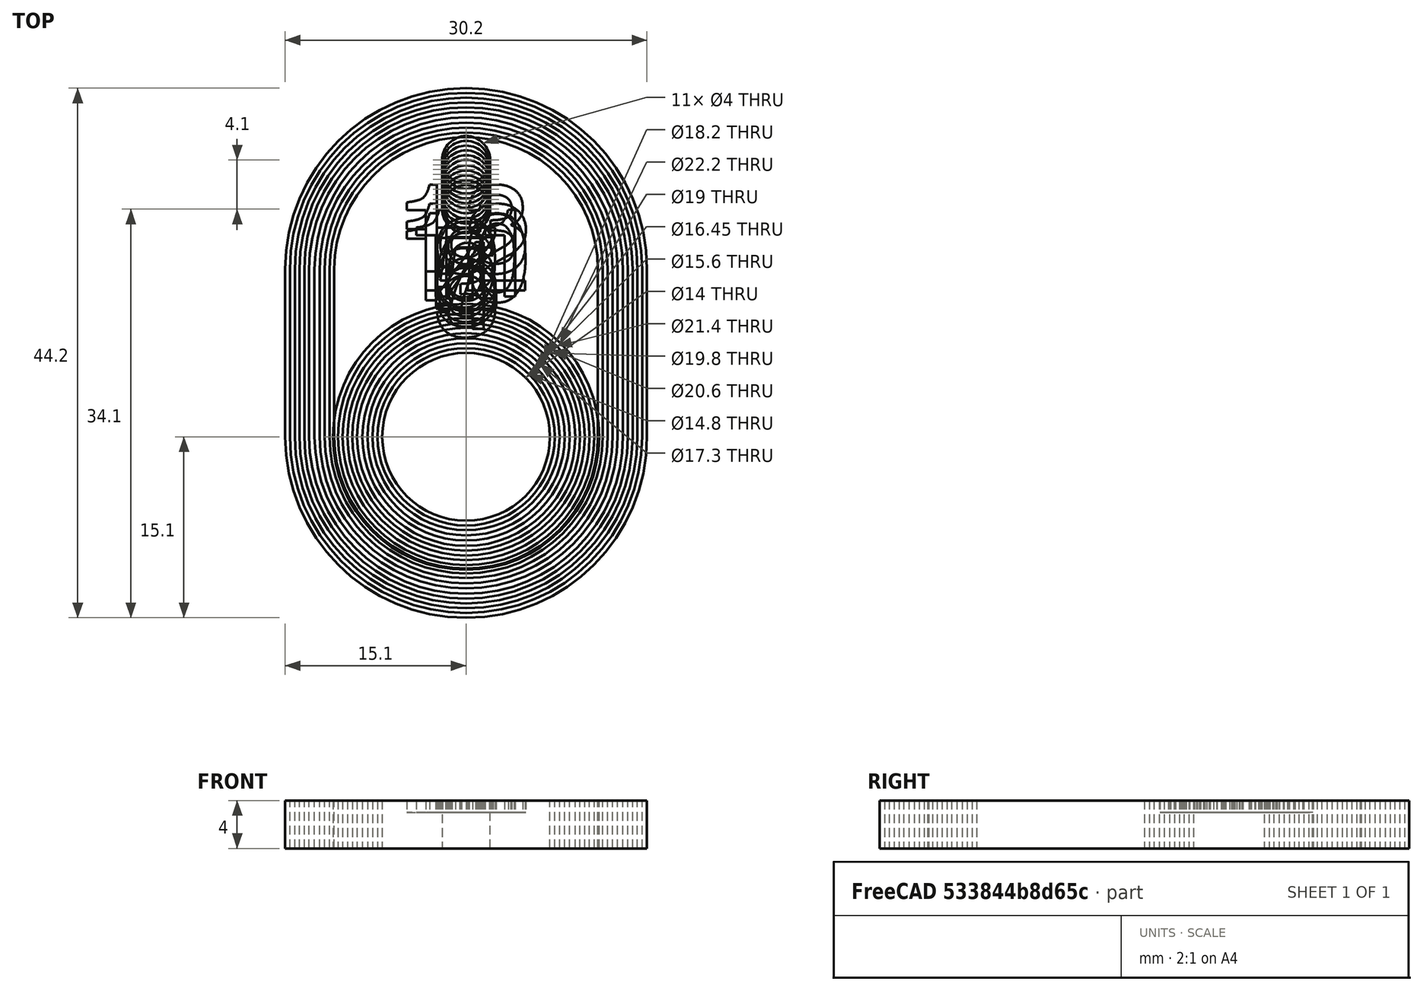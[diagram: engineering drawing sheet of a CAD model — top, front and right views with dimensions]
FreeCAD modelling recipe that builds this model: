
FCSTD DOCUMENT  (FreeCAD 0.18R16146 (Git))
Label: Ring-Gauges
License: All rights reserved
LicenseURL: http://en.wikipedia.org/wiki/All_rights_reserved
objects: Sketcher::SketchObject×22, PartDesign::Pad×11, PartDesign::Pocket×11, PartDesign::Body×11, Mesh::Feature×11, Part::Part2DObjectPython×1
note: 78 computed .brp shape members not serialized (recipe doc carries the construction recipe); baked Part::Feature solids carry a one-line shape summary decoded from their .brp

FEATURE [Sketcher::SketchObject] Sketch  label="Sketch13"
  MapMode = 5
  Support = -> [XY_Plane]
  sketch-geometry (11):
    g0: ArcOfCircle CenterX=-3.8225e-12 CenterY=14 CenterZ=0 NormalX=0 NormalY=0 NormalZ=1 AngleXU=0 Radius=15.1 StartAngle=2.08319e-11 EndAngle=3.14159
    g1: ArcOfCircle CenterX=0 CenterY=0 CenterZ=0 NormalX=0 NormalY=0 NormalZ=1 AngleXU=0 Radius=15.1 StartAngle=3.14159 EndAngle=6.28319
    g2: LineSegment StartX=-15.1 StartY=14 StartZ=0 EndX=-15.1 EndY=-6.47553e-11 EndZ=0
    g3: LineSegment StartX=15.1 StartY=14 StartZ=0 EndX=15.1 EndY=5.34051e-10 EndZ=0
    g4: Circle CenterX=0 CenterY=0 CenterZ=0 NormalX=0 NormalY=0 NormalZ=1 AngleXU=0 Radius=11.1
    g5: Circle CenterX=0 CenterY=23.1 CenterZ=0 NormalX=0 NormalY=0 NormalZ=1 AngleXU=0 Radius=2
    g6: GeomPoint X=0 Y=11.1 Z=0
    g7: GeomPoint X=0 Y=21.1 Z=0
    g8: GeomPoint X=0 Y=29.1 Z=0
    g9: GeomPoint X=0 Y=25.1 Z=0
    g10: GeomPoint X=-11.1 Y=-6.47556e-11 Z=0
  constraints (24):
    c: Tangent(g0,g3) = 1.5708
    c: Tangent(g0,g2) = -1.5708
    c: Tangent(g2,g1) = -1.5708
    c: Tangent(g3,g1) = 1.5708
    c: Vertical(g2)
    c: Equal(g0,g1)
    c: Coincident(g4,g1)
    c: Diameter(g5) = 4
    c: PointOnObject(g6,g4)
    c: Vertical(g6,g1)
    c: PointOnObject(g7,g5)
    c: Vertical(g7,g5)
    c: Vertical(g5,g1)
    c: PointOnObject(g8,g0)
    c: Vertical(g8,g1)
    c: PointOnObject(g9,g5)
    c: Vertical(g9,g5)
    c: DistanceY(g9,g8) = 4
    c: PointOnObject(g10,g4)
    c: Horizontal(g10,g1)
    c: DistanceX(g1,g10) = 4
    c: Diameter(g4) = 22.2
    c: DistanceY(g6,g7) = 10
    c: Coincident(g1,g-1)
FEATURE [PartDesign::Pad] Pad  label="Pad13"
  Length = 4
  Length2 = 100
  Profile = -> Sketch
  Type = 0
FEATURE [Sketcher::SketchObject] Sketch001  label="Sketch12"
  MapMode = 5
  Support = -> [XY_Plane001]
  sketch-geometry (11):
    g0: ArcOfCircle CenterX=-3.88e-14 CenterY=14 CenterZ=0 NormalX=0 NormalY=0 NormalZ=1 AngleXU=0 Radius=14.7 StartAngle=-2.93e-14 EndAngle=3.14159
    g1: ArcOfCircle CenterX=0 CenterY=0 CenterZ=0 NormalX=0 NormalY=0 NormalZ=1 AngleXU=0 Radius=14.7 StartAngle=3.14159 EndAngle=6.28319
    g2: LineSegment StartX=-14.7 StartY=14 StartZ=0 EndX=-14.7 EndY=-2.611e-13 EndZ=0
    g3: LineSegment StartX=14.7 StartY=14 StartZ=0 EndX=14.7 EndY=-7.567e-13 EndZ=0
    g4: Circle CenterX=0 CenterY=0 CenterZ=0 NormalX=0 NormalY=0 NormalZ=1 AngleXU=0 Radius=10.7
    g5: Circle CenterX=0 CenterY=22.7 CenterZ=0 NormalX=0 NormalY=0 NormalZ=1 AngleXU=0 Radius=2
    g6: GeomPoint X=0 Y=10.7 Z=0
    g7: GeomPoint X=0 Y=20.7 Z=0
    g8: GeomPoint X=0 Y=28.7 Z=0
    g9: GeomPoint X=0 Y=24.7 Z=0
    g10: GeomPoint X=-10.7 Y=-2.611e-13 Z=0
  constraints (24):
    c: Tangent(g0,g3) = 1.5708
    c: Tangent(g0,g2) = -1.5708
    c: Tangent(g2,g1) = -1.5708
    c: Tangent(g3,g1) = 1.5708
    c: Vertical(g2)
    c: Equal(g0,g1)
    c: Coincident(g4,g1)
    c: Diameter(g5) = 4
    c: PointOnObject(g6,g4)
    c: Vertical(g6,g1)
    c: PointOnObject(g7,g5)
    c: Vertical(g7,g5)
    c: Vertical(g5,g1)
    c: PointOnObject(g8,g0)
    c: Vertical(g8,g1)
    c: PointOnObject(g9,g5)
    c: Vertical(g9,g5)
    c: DistanceY(g9,g8) = 4
    c: PointOnObject(g10,g4)
    c: Horizontal(g10,g1)
    c: DistanceX(g1,g10) = 4
    c: Diameter(g4) = 21.4
    c: DistanceY(g6,g7) = 10
    c: Coincident(g1,g-1)
FEATURE [PartDesign::Pad] Pad001  label="Pad12"
  Length = 4
  Length2 = 100
  Profile = -> Sketch001
  Type = 0
FEATURE [Sketcher::SketchObject] Sketch002  label="Sketch11"
  MapMode = 5
  Support = -> [XY_Plane002]
  sketch-geometry (11):
    g0: ArcOfCircle CenterX=8e-16 CenterY=14 CenterZ=0 NormalX=0 NormalY=0 NormalZ=1 AngleXU=0 Radius=14.3 StartAngle=1e-16 EndAngle=3.14159
    g1: ArcOfCircle CenterX=0 CenterY=0 CenterZ=0 NormalX=0 NormalY=0 NormalZ=1 AngleXU=0 Radius=14.3 StartAngle=3.14159 EndAngle=6.28319
    g2: LineSegment StartX=-14.3 StartY=14 StartZ=0 EndX=-14.3 EndY=0 EndZ=0
    g3: LineSegment StartX=14.3 StartY=14 StartZ=0 EndX=14.3 EndY=-1.8e-15 EndZ=0
    g4: Circle CenterX=0 CenterY=0 CenterZ=0 NormalX=0 NormalY=0 NormalZ=1 AngleXU=0 Radius=10.3
    g5: Circle CenterX=0 CenterY=22.3 CenterZ=0 NormalX=0 NormalY=0 NormalZ=1 AngleXU=0 Radius=2
    g6: GeomPoint X=0 Y=10.3 Z=0
    g7: GeomPoint X=0 Y=20.3 Z=0
    g8: GeomPoint X=0 Y=28.3 Z=0
    g9: GeomPoint X=0 Y=24.3 Z=0
    g10: GeomPoint X=-10.3 Y=0 Z=0
  constraints (24):
    c: Tangent(g0,g3) = 1.5708
    c: Tangent(g0,g2) = -1.5708
    c: Tangent(g2,g1) = -1.5708
    c: Tangent(g3,g1) = 1.5708
    c: Vertical(g2)
    c: Equal(g0,g1)
    c: Coincident(g4,g1)
    c: Diameter(g5) = 4
    c: PointOnObject(g6,g4)
    c: Vertical(g6,g1)
    c: PointOnObject(g7,g5)
    c: Vertical(g7,g5)
    c: Vertical(g5,g1)
    c: PointOnObject(g8,g0)
    c: Vertical(g8,g1)
    c: PointOnObject(g9,g5)
    c: Vertical(g9,g5)
    c: DistanceY(g9,g8) = 4
    c: PointOnObject(g10,g4)
    c: Horizontal(g10,g1)
    c: DistanceX(g1,g10) = 4
    c: Diameter(g4) = 20.6
    c: DistanceY(g6,g7) = 10
    c: Coincident(g1,g-1)
FEATURE [PartDesign::Pad] Pad003  label="Pad11"
  Length = 4
  Length2 = 100
  Profile = -> Sketch002
  Type = 0
FEATURE [Sketcher::SketchObject] Sketch003  label="Sketch10"
  MapMode = 5
  Support = -> [XY_Plane003]
  sketch-geometry (11):
    g0: ArcOfCircle CenterX=-3.3e-15 CenterY=14 CenterZ=0 NormalX=0 NormalY=0 NormalZ=1 AngleXU=0 Radius=13.9 StartAngle=-1.8e-15 EndAngle=3.14159
    g1: ArcOfCircle CenterX=0 CenterY=0 CenterZ=0 NormalX=0 NormalY=0 NormalZ=1 AngleXU=0 Radius=13.9 StartAngle=3.14159 EndAngle=6.28319
    g2: LineSegment StartX=-13.9 StartY=14 StartZ=0 EndX=-13.9 EndY=-2.66e-14 EndZ=0
    g3: LineSegment StartX=13.9 StartY=14 StartZ=0 EndX=13.9 EndY=-5.33e-14 EndZ=0
    g4: Circle CenterX=0 CenterY=0 CenterZ=0 NormalX=0 NormalY=0 NormalZ=1 AngleXU=0 Radius=9.9
    g5: Circle CenterX=0 CenterY=21.9 CenterZ=0 NormalX=0 NormalY=0 NormalZ=1 AngleXU=0 Radius=2
    g6: GeomPoint X=0 Y=9.9 Z=0
    g7: GeomPoint X=0 Y=19.9 Z=0
    g8: GeomPoint X=0 Y=27.9 Z=0
    g9: GeomPoint X=0 Y=23.9 Z=0
    g10: GeomPoint X=-9.9 Y=-2.66e-14 Z=0
  constraints (24):
    c: Tangent(g0,g3) = 1.5708
    c: Tangent(g0,g2) = -1.5708
    c: Tangent(g2,g1) = -1.5708
    c: Tangent(g3,g1) = 1.5708
    c: Vertical(g2)
    c: Equal(g0,g1)
    c: Coincident(g4,g1)
    c: Diameter(g5) = 4
    c: PointOnObject(g6,g4)
    c: Vertical(g6,g1)
    c: PointOnObject(g7,g5)
    c: Vertical(g7,g5)
    c: Vertical(g5,g1)
    c: PointOnObject(g8,g0)
    c: Vertical(g8,g1)
    c: PointOnObject(g9,g5)
    c: Vertical(g9,g5)
    c: DistanceY(g9,g8) = 4
    c: PointOnObject(g10,g4)
    c: Horizontal(g10,g1)
    c: DistanceX(g1,g10) = 4
    c: Diameter(g4) = 19.8
    c: DistanceY(g6,g7) = 10
    c: Coincident(g1,g-1)
FEATURE [PartDesign::Pad] Pad002  label="Pad10"
  Length = 4
  Length2 = 100
  Profile = -> Sketch003
  Type = 0
FEATURE [Sketcher::SketchObject] Sketch004  label="Sketch9"
  MapMode = 5
  Support = -> [XY_Plane004]
  sketch-geometry (11):
    g0: ArcOfCircle CenterX=-5e-16 CenterY=14 CenterZ=0 NormalX=0 NormalY=0 NormalZ=1 AngleXU=0 Radius=13.5 StartAngle=1e-16 EndAngle=3.14159
    g1: ArcOfCircle CenterX=0 CenterY=0 CenterZ=0 NormalX=0 NormalY=0 NormalZ=1 AngleXU=0 Radius=13.5 StartAngle=3.14159 EndAngle=6.28319
    g2: LineSegment StartX=-13.5 StartY=14 StartZ=0 EndX=-13.5 EndY=0 EndZ=0
    g3: LineSegment StartX=13.5 StartY=14 StartZ=0 EndX=13.5 EndY=-1.8e-15 EndZ=0
    g4: Circle CenterX=0 CenterY=0 CenterZ=0 NormalX=0 NormalY=0 NormalZ=1 AngleXU=0 Radius=9.5
    g5: Circle CenterX=0 CenterY=21.5 CenterZ=0 NormalX=0 NormalY=0 NormalZ=1 AngleXU=0 Radius=2
    g6: GeomPoint X=0 Y=9.5 Z=0
    g7: GeomPoint X=0 Y=19.5 Z=0
    g8: GeomPoint X=0 Y=27.5 Z=0
    g9: GeomPoint X=0 Y=23.5 Z=0
    g10: GeomPoint X=-9.5 Y=0 Z=0
  constraints (24):
    c: Tangent(g0,g3) = 1.5708
    c: Tangent(g0,g2) = -1.5708
    c: Tangent(g2,g1) = -1.5708
    c: Tangent(g3,g1) = 1.5708
    c: Vertical(g2)
    c: Equal(g0,g1)
    c: Coincident(g4,g1)
    c: Diameter(g5) = 4
    c: PointOnObject(g6,g4)
    c: Vertical(g6,g1)
    c: PointOnObject(g7,g5)
    c: Vertical(g7,g5)
    c: Vertical(g5,g1)
    c: PointOnObject(g8,g0)
    c: Vertical(g8,g1)
    c: PointOnObject(g9,g5)
    c: Vertical(g9,g5)
    c: DistanceY(g9,g8) = 4
    c: PointOnObject(g10,g4)
    c: Horizontal(g10,g1)
    c: DistanceX(g1,g10) = 4
    c: Diameter(g4) = 19
    c: DistanceY(g6,g7) = 10
    c: Coincident(g1,g-1)
FEATURE [PartDesign::Pad] Pad005  label="Pad9"
  Length = 4
  Length2 = 100
  Profile = -> Sketch004
  Type = 0
FEATURE [Sketcher::SketchObject] Sketch005  label="Sketch8"
  MapMode = 5
  Support = -> [XY_Plane005]
  sketch-geometry (11):
    g0: ArcOfCircle CenterX=5e-16 CenterY=14 CenterZ=0 NormalX=0 NormalY=0 NormalZ=1 AngleXU=0 Radius=13.1 StartAngle=1e-16 EndAngle=3.14159
    g1: ArcOfCircle CenterX=0 CenterY=0 CenterZ=0 NormalX=0 NormalY=0 NormalZ=1 AngleXU=0 Radius=13.1 StartAngle=3.14159 EndAngle=6.28319
    g2: LineSegment StartX=-13.1 StartY=14 StartZ=0 EndX=-13.1 EndY=0 EndZ=0
    g3: LineSegment StartX=13.1 StartY=14 StartZ=0 EndX=13.1 EndY=-3.6e-15 EndZ=0
    g4: Circle CenterX=0 CenterY=0 CenterZ=0 NormalX=0 NormalY=0 NormalZ=1 AngleXU=0 Radius=9.1
    g5: Circle CenterX=0 CenterY=21.1 CenterZ=0 NormalX=0 NormalY=0 NormalZ=1 AngleXU=0 Radius=2
    g6: GeomPoint X=0 Y=9.1 Z=0
    g7: GeomPoint X=0 Y=19.1 Z=0
    g8: GeomPoint X=0 Y=27.1 Z=0
    g9: GeomPoint X=0 Y=23.1 Z=0
    g10: GeomPoint X=-9.1 Y=0 Z=0
  constraints (24):
    c: Tangent(g0,g3) = 1.5708
    c: Tangent(g0,g2) = -1.5708
    c: Tangent(g2,g1) = -1.5708
    c: Tangent(g3,g1) = 1.5708
    c: Vertical(g2)
    c: Equal(g0,g1)
    c: Coincident(g4,g1)
    c: Diameter(g5) = 4
    c: PointOnObject(g6,g4)
    c: Vertical(g6,g1)
    c: PointOnObject(g7,g5)
    c: Vertical(g7,g5)
    c: Vertical(g5,g1)
    c: PointOnObject(g8,g0)
    c: Vertical(g8,g1)
    c: PointOnObject(g9,g5)
    c: Vertical(g9,g5)
    c: DistanceY(g9,g8) = 4
    c: PointOnObject(g10,g4)
    c: Horizontal(g10,g1)
    c: DistanceX(g1,g10) = 4
    c: Diameter(g4) = 18.2
    c: DistanceY(g6,g7) = 10
    c: Coincident(g1,g-1)
FEATURE [PartDesign::Pad] Pad004  label="Pad8"
  Length = 4
  Length2 = 100
  Profile = -> Sketch005
  Type = 0
FEATURE [Sketcher::SketchObject] Sketch006  label="Sketch7"
  MapMode = 5
  Support = -> [XY_Plane006]
  sketch-geometry (11):
    g0: ArcOfCircle CenterX=0 CenterY=14 CenterZ=0 NormalX=0 NormalY=0 NormalZ=1 AngleXU=0 Radius=12.65 StartAngle=0 EndAngle=3.14159
    g1: ArcOfCircle CenterX=0 CenterY=0 CenterZ=0 NormalX=0 NormalY=0 NormalZ=1 AngleXU=0 Radius=12.65 StartAngle=3.14159 EndAngle=6.28319
    g2: LineSegment StartX=-12.65 StartY=14 StartZ=0 EndX=-12.65 EndY=1.8e-15 EndZ=0
    g3: LineSegment StartX=12.65 StartY=14 StartZ=0 EndX=12.65 EndY=-3.6e-15 EndZ=0
    g4: Circle CenterX=0 CenterY=0 CenterZ=0 NormalX=0 NormalY=0 NormalZ=1 AngleXU=0 Radius=8.65
    g5: Circle CenterX=0 CenterY=20.65 CenterZ=0 NormalX=0 NormalY=0 NormalZ=1 AngleXU=0 Radius=2
    g6: GeomPoint X=0 Y=8.65 Z=0
    g7: GeomPoint X=0 Y=18.65 Z=0
    g8: GeomPoint X=0 Y=26.65 Z=0
    g9: GeomPoint X=0 Y=22.65 Z=0
    g10: GeomPoint X=-8.65 Y=1.5e-15 Z=0
  constraints (24):
    c: Tangent(g0,g3) = 1.5708
    c: Tangent(g0,g2) = -1.5708
    c: Tangent(g2,g1) = -1.5708
    c: Tangent(g3,g1) = 1.5708
    c: Vertical(g2)
    c: Equal(g0,g1)
    c: Coincident(g4,g1)
    c: Diameter(g5) = 4
    c: PointOnObject(g6,g4)
    c: Vertical(g6,g1)
    c: PointOnObject(g7,g5)
    c: Vertical(g7,g5)
    c: Vertical(g5,g1)
    c: PointOnObject(g8,g0)
    c: Vertical(g8,g1)
    c: PointOnObject(g9,g5)
    c: Vertical(g9,g5)
    c: DistanceY(g9,g8) = 4
    c: PointOnObject(g10,g4)
    c: Horizontal(g10,g1)
    c: DistanceX(g1,g10) = 4
    c: Diameter(g4) = 17.3
    c: DistanceY(g6,g7) = 10
    c: Coincident(g1,g-1)
FEATURE [PartDesign::Pad] Pad007  label="Pad7"
  Length = 4
  Length2 = 100
  Profile = -> Sketch006
  Type = 0
FEATURE [Sketcher::SketchObject] Sketch007  label="Sketch6"
  MapMode = 5
  Support = -> [XY_Plane007]
  sketch-geometry (11):
    g0: ArcOfCircle CenterX=-1.3e-15 CenterY=14 CenterZ=0 NormalX=0 NormalY=0 NormalZ=1 AngleXU=0 Radius=12.225 StartAngle=-3.6e-15 EndAngle=3.14159
    g1: ArcOfCircle CenterX=0 CenterY=0 CenterZ=0 NormalX=0 NormalY=0 NormalZ=1 AngleXU=0 Radius=12.225 StartAngle=3.14159 EndAngle=6.28319
    g2: LineSegment StartX=-12.225 StartY=14 StartZ=0 EndX=-12.225 EndY=1.8e-15 EndZ=0
    g3: LineSegment StartX=12.225 StartY=14 StartZ=0 EndX=12.225 EndY=-4.62e-14 EndZ=0
    g4: Circle CenterX=0 CenterY=0 CenterZ=0 NormalX=0 NormalY=0 NormalZ=1 AngleXU=0 Radius=8.225
    g5: Circle CenterX=0 CenterY=20.225 CenterZ=0 NormalX=0 NormalY=0 NormalZ=1 AngleXU=0 Radius=2
    g6: GeomPoint X=0 Y=8.225 Z=0
    g7: GeomPoint X=0 Y=18.225 Z=0
    g8: GeomPoint X=0 Y=26.225 Z=0
    g9: GeomPoint X=0 Y=22.225 Z=0
    g10: GeomPoint X=-8.225 Y=1.5e-15 Z=0
  constraints (24):
    c: Tangent(g0,g3) = 1.5708
    c: Tangent(g0,g2) = -1.5708
    c: Tangent(g2,g1) = -1.5708
    c: Tangent(g3,g1) = 1.5708
    c: Vertical(g2)
    c: Equal(g0,g1)
    c: Coincident(g4,g1)
    c: Diameter(g5) = 4
    c: PointOnObject(g6,g4)
    c: Vertical(g6,g1)
    c: PointOnObject(g7,g5)
    c: Vertical(g7,g5)
    c: Vertical(g5,g1)
    c: PointOnObject(g8,g0)
    c: Vertical(g8,g1)
    c: PointOnObject(g9,g5)
    c: Vertical(g9,g5)
    c: DistanceY(g9,g8) = 4
    c: PointOnObject(g10,g4)
    c: Horizontal(g10,g1)
    c: DistanceX(g1,g10) = 4
    c: Diameter(g4) = 16.45
    c: DistanceY(g6,g7) = 10
    c: Coincident(g1,g-1)
FEATURE [PartDesign::Pad] Pad006  label="Pad6"
  Length = 4
  Length2 = 100
  Profile = -> Sketch007
  Type = 0
FEATURE [Sketcher::SketchObject] Sketch008  label="Sketch5"
  MapMode = 5
  Support = -> [XY_Plane008]
  sketch-geometry (11):
    g0: ArcOfCircle CenterX=-4.8e-15 CenterY=14 CenterZ=0 NormalX=0 NormalY=0 NormalZ=1 AngleXU=0 Radius=11.8 StartAngle=-4.09e-14 EndAngle=3.14159
    g1: ArcOfCircle CenterX=0 CenterY=0 CenterZ=0 NormalX=0 NormalY=0 NormalZ=1 AngleXU=0 Radius=11.8 StartAngle=3.14159 EndAngle=6.28319
    g2: LineSegment StartX=-11.8 StartY=14 StartZ=0 EndX=-11.8 EndY=4.8e-14 EndZ=0
    g3: LineSegment StartX=11.8 StartY=14 StartZ=0 EndX=11.8 EndY=-2.167e-13 EndZ=0
    g4: Circle CenterX=0 CenterY=0 CenterZ=0 NormalX=0 NormalY=0 NormalZ=1 AngleXU=0 Radius=7.8
    g5: Circle CenterX=0 CenterY=19.8 CenterZ=0 NormalX=0 NormalY=0 NormalZ=1 AngleXU=0 Radius=2
    g6: GeomPoint X=0 Y=7.8 Z=0
    g7: GeomPoint X=0 Y=17.8 Z=0
    g8: GeomPoint X=0 Y=25.8 Z=0
    g9: GeomPoint X=0 Y=21.8 Z=0
    g10: GeomPoint X=-7.8 Y=4.86e-14 Z=0
  constraints (24):
    c: Tangent(g0,g3) = 1.5708
    c: Tangent(g0,g2) = -1.5708
    c: Tangent(g2,g1) = -1.5708
    c: Tangent(g3,g1) = 1.5708
    c: Vertical(g2)
    c: Equal(g0,g1)
    c: Coincident(g4,g1)
    c: Diameter(g5) = 4
    c: PointOnObject(g6,g4)
    c: Vertical(g6,g1)
    c: PointOnObject(g7,g5)
    c: Vertical(g7,g5)
    c: Vertical(g5,g1)
    c: PointOnObject(g8,g0)
    c: Vertical(g8,g1)
    c: PointOnObject(g9,g5)
    c: Vertical(g9,g5)
    c: DistanceY(g9,g8) = 4
    c: PointOnObject(g10,g4)
    c: Horizontal(g10,g1)
    c: DistanceX(g1,g10) = 4
    c: Diameter(g4) = 15.6
    c: DistanceY(g6,g7) = 10
    c: Coincident(g1,g-1)
FEATURE [PartDesign::Pad] Pad009  label="Pad5"
  Length = 4
  Length2 = 100
  Profile = -> Sketch008
  Type = 0
FEATURE [Sketcher::SketchObject] Sketch009  label="Sketch4"
  MapMode = 5
  Support = -> [XY_Plane009]
  sketch-geometry (11):
    g0: ArcOfCircle CenterX=-5e-16 CenterY=14 CenterZ=0 NormalX=0 NormalY=0 NormalZ=1 AngleXU=0 Radius=11.4 StartAngle=1e-16 EndAngle=3.14159
    g1: ArcOfCircle CenterX=0 CenterY=0 CenterZ=0 NormalX=0 NormalY=0 NormalZ=1 AngleXU=0 Radius=11.4 StartAngle=3.14159 EndAngle=6.28319
    g2: LineSegment StartX=-11.4 StartY=14 StartZ=0 EndX=-11.4 EndY=0 EndZ=0
    g3: LineSegment StartX=11.4 StartY=14 StartZ=0 EndX=11.4 EndY=-3.6e-15 EndZ=0
    g4: Circle CenterX=0 CenterY=0 CenterZ=0 NormalX=0 NormalY=0 NormalZ=1 AngleXU=0 Radius=7.4
    g5: Circle CenterX=0 CenterY=19.4 CenterZ=0 NormalX=0 NormalY=0 NormalZ=1 AngleXU=0 Radius=2
    g6: GeomPoint X=0 Y=7.4 Z=0
    g7: GeomPoint X=0 Y=17.4 Z=0
    g8: GeomPoint X=0 Y=25.4 Z=0
    g9: GeomPoint X=0 Y=21.4 Z=0
    g10: GeomPoint X=-7.4 Y=0 Z=0
  constraints (24):
    c: Tangent(g0,g3) = 1.5708
    c: Tangent(g0,g2) = -1.5708
    c: Tangent(g2,g1) = -1.5708
    c: Tangent(g3,g1) = 1.5708
    c: Vertical(g2)
    c: Equal(g0,g1)
    c: Coincident(g4,g1)
    c: Diameter(g5) = 4
    c: PointOnObject(g6,g4)
    c: Vertical(g6,g1)
    c: PointOnObject(g7,g5)
    c: Vertical(g7,g5)
    c: Vertical(g5,g1)
    c: PointOnObject(g8,g0)
    c: Vertical(g8,g1)
    c: PointOnObject(g9,g5)
    c: Vertical(g9,g5)
    c: DistanceY(g9,g8) = 4
    c: PointOnObject(g10,g4)
    c: Horizontal(g10,g1)
    c: DistanceX(g1,g10) = 4
    c: Diameter(g4) = 14.8
    c: DistanceY(g6,g7) = 10
    c: Coincident(g1,g-1)
FEATURE [PartDesign::Pad] Pad008  label="Pad4"
  Length = 4
  Length2 = 100
  Profile = -> Sketch009
  Type = 0
FEATURE [Sketcher::SketchObject] Sketch010  label="Sketch3"
  MapMode = 5
  Support = -> [XY_Plane010]
  sketch-geometry (11):
    g0: ArcOfCircle CenterX=3e-16 CenterY=14 CenterZ=0 NormalX=0 NormalY=0 NormalZ=1 AngleXU=0 Radius=11 StartAngle=3.8e-15 EndAngle=3.14159
    g1: ArcOfCircle CenterX=0 CenterY=0 CenterZ=0 NormalX=0 NormalY=0 NormalZ=1 AngleXU=0 Radius=11 StartAngle=3.14159 EndAngle=6.28319
    g2: LineSegment StartX=-11 StartY=14 StartZ=0 EndX=-11 EndY=0 EndZ=0
    g3: LineSegment StartX=11 StartY=14 StartZ=0 EndX=11 EndY=7.1e-15 EndZ=0
    g4: Circle CenterX=0 CenterY=0 CenterZ=0 NormalX=0 NormalY=0 NormalZ=1 AngleXU=0 Radius=7
    g5: Circle CenterX=0 CenterY=19 CenterZ=0 NormalX=0 NormalY=0 NormalZ=1 AngleXU=0 Radius=2
    g6: GeomPoint X=0 Y=7 Z=0
    g7: GeomPoint X=0 Y=17 Z=0
    g8: GeomPoint X=0 Y=25 Z=0
    g9: GeomPoint X=0 Y=21 Z=0
    g10: GeomPoint X=-7 Y=5e-16 Z=0
  constraints (24):
    c: Tangent(g0,g3) = 1.5708
    c: Tangent(g0,g2) = -1.5708
    c: Tangent(g2,g1) = -1.5708
    c: Tangent(g3,g1) = 1.5708
    c: Vertical(g2)
    c: Equal(g0,g1)
    c: Coincident(g4,g1)
    c: Diameter(g5) = 4
    c: PointOnObject(g6,g4)
    c: Vertical(g6,g1)
    c: PointOnObject(g7,g5)
    c: Vertical(g7,g5)
    c: Vertical(g5,g1)
    c: PointOnObject(g8,g0)
    c: Vertical(g8,g1)
    c: PointOnObject(g9,g5)
    c: Vertical(g9,g5)
    c: DistanceY(g9,g8) = 4
    c: PointOnObject(g10,g4)
    c: Horizontal(g10,g1)
    c: DistanceX(g1,g10) = 4
    c: Diameter(g4) = 14
    c: DistanceY(g6,g7) = 10
    c: Coincident(g1,g-1)
FEATURE [PartDesign::Pad] Pad011  label="Pad3"
  Length = 4
  Length2 = 100
  Profile = -> Sketch010
  Type = 0
FEATURE [Part::Part2DObjectPython] ShapeString  label="Draft-Number"  # Draft 2D object (typed FeaturePython)
  FontFile = <path>
  Placement = pos=(-30,20,0) rot=(0,0,1;0rad)
  Size = 4
  String = 13
  Tracking = 0
FEATURE [Sketcher::SketchObject] CopySketch011  label="Num3"
  Placement = pos=(27.25,-11.5,4) rot=(0,0,1;0rad)
  sketch-geometry (25):
    g0: BSplineCurve PolesCount=3 KnotsCount=2 Degree=2 IsPeriodic=0
    g1: BSplineCurve PolesCount=3 KnotsCount=2 Degree=2 IsPeriodic=0
    g2: BSplineCurve PolesCount=3 KnotsCount=2 Degree=2 IsPeriodic=0
    g3: BSplineCurve PolesCount=3 KnotsCount=2 Degree=2 IsPeriodic=0
    g4: BSplineCurve PolesCount=3 KnotsCount=2 Degree=2 IsPeriodic=0
    g5: LineSegment StartX=-27.7367 StartY=23.4133 StartZ=0 EndX=-27.7367 EndY=24.2667 EndZ=0
    g6: LineSegment StartX=-27.6233 StartY=23.4133 StartZ=0 EndX=-27.7367 EndY=23.4133 EndZ=0
    g7: LineSegment StartX=-27.2433 StartY=23.4233 StartZ=0 EndX=-27.6233 EndY=23.4133 EndZ=0
    g8: BSplineCurve PolesCount=3 KnotsCount=2 Degree=2 IsPeriodic=0
    g9: BSplineCurve PolesCount=3 KnotsCount=2 Degree=2 IsPeriodic=0
    g10: BSplineCurve PolesCount=3 KnotsCount=2 Degree=2 IsPeriodic=0
    g11: BSplineCurve PolesCount=3 KnotsCount=2 Degree=2 IsPeriodic=0
    g12: BSplineCurve PolesCount=3 KnotsCount=2 Degree=2 IsPeriodic=0
    g13: LineSegment StartX=-29.6733 StartY=21.92 StartZ=0 EndX=-28.77 EndY=21.92 EndZ=0
    g14: BSplineCurve PolesCount=3 KnotsCount=2 Degree=2 IsPeriodic=0
    g15: BSplineCurve PolesCount=3 KnotsCount=2 Degree=2 IsPeriodic=0
    g16: BSplineCurve PolesCount=3 KnotsCount=2 Degree=2 IsPeriodic=0
    g17: BSplineCurve PolesCount=3 KnotsCount=2 Degree=2 IsPeriodic=0
    g18: BSplineCurve PolesCount=3 KnotsCount=2 Degree=2 IsPeriodic=0
    g19: BSplineCurve PolesCount=3 KnotsCount=2 Degree=2 IsPeriodic=0
    g20: BSplineCurve PolesCount=3 KnotsCount=2 Degree=2 IsPeriodic=0
    g21: BSplineCurve PolesCount=3 KnotsCount=2 Degree=2 IsPeriodic=0
    g22: BSplineCurve PolesCount=3 KnotsCount=2 Degree=2 IsPeriodic=0
    g23: LineSegment StartX=-28.6167 StartY=25.12 StartZ=0 EndX=-29.52 EndY=25.12 EndZ=0
    g24: BSplineCurve PolesCount=3 KnotsCount=2 Degree=2 IsPeriodic=0
  constraints (29):
    c: Coincident(g0,g1)
    c: Coincident(g1,g2)
    c: Coincident(g2,g3)
    c: Coincident(g3,g4)
    c: Coincident(g4,g5)
    c: Vertical(g5)
    c: Coincident(g5,g6)
    c: Horizontal(g6)
    c: Coincident(g6,g7)
    c: Coincident(g7,g8)
    c: Coincident(g8,g9)
    c: Coincident(g9,g10)
    c: Coincident(g10,g11)
    c: Coincident(g11,g12)
    c: Coincident(g12,g13)
    c: Horizontal(g13)
    c: Coincident(g13,g14)
    c: Coincident(g14,g15)
    c: Coincident(g15,g16)
    c: Coincident(g16,g17)
    c: Coincident(g17,g18)
    c: Coincident(g18,g19)
    c: Coincident(g19,g20)
    c: Coincident(g20,g21)
    c: Coincident(g21,g22)
    c: Coincident(g22,g23)
    c: Horizontal(g23)
    c: Coincident(g23,g24)
    c: Coincident(g24,g0)
FEATURE [PartDesign::Pocket] Pocket  label="Pocket3"
  BaseFeature = -> Pad011
  Length = 1
  Length2 = 100
  Profile = -> CopySketch011
  Type = 0
FEATURE [PartDesign::Body] Body010  label="Size-3"
  Group = -> [Sketch010,Pad011,Pocket]
  Origin = -> Origin010
  Tip = -> Pocket
FEATURE [Sketcher::SketchObject] Sketch011  label="Num4"
  AttachmentOffset = pos=(27.2,-11,0) rot=(0,0,1;0rad)
  MapMode = 5
  Placement = pos=(27.2,-11,4) rot=(0,0,1;0rad)
  Support = -> [Pad008]
  sketch-geometry (14):
    g0: LineSegment StartX=-26.65 StartY=21.7067 StartZ=0 EndX=-29.7133 EndY=21.7067 EndZ=0
    g1: LineSegment StartX=-26.65 StartY=20 StartZ=0 EndX=-26.65 EndY=21.7067 EndZ=0
    g2: LineSegment StartX=-25.75 StartY=20 StartZ=0 EndX=-26.65 EndY=20 EndZ=0
    g3: LineSegment StartX=-25.75 StartY=21.7067 StartZ=0 EndX=-25.75 EndY=20 EndZ=0
    g4: LineSegment StartX=-24.6767 StartY=21.7067 StartZ=0 EndX=-25.75 EndY=21.7067 EndZ=0
    g5: LineSegment StartX=-24.6767 StartY=22.56 StartZ=0 EndX=-24.6767 EndY=21.7067 EndZ=0
    g6: LineSegment StartX=-25.75 StartY=22.56 StartZ=0 EndX=-24.6767 EndY=22.56 EndZ=0
    g7: LineSegment StartX=-25.75 StartY=27.2533 StartZ=0 EndX=-25.75 EndY=22.56 EndZ=0
    g8: LineSegment StartX=-26.4167 StartY=27.2533 StartZ=0 EndX=-25.75 EndY=27.2533 EndZ=0
    g9: LineSegment StartX=-29.7133 StartY=22.7033 StartZ=0 EndX=-26.4167 EndY=27.2533 EndZ=0
    g10: LineSegment StartX=-29.7133 StartY=21.7067 StartZ=0 EndX=-29.7133 EndY=22.7033 EndZ=0
    g11: LineSegment StartX=-26.65 StartY=22.56 StartZ=0 EndX=-26.65 EndY=25.7233 EndZ=0
    g12: LineSegment StartX=-28.9233 StartY=22.56 StartZ=0 EndX=-26.65 EndY=22.56 EndZ=0
    g13: LineSegment StartX=-26.65 StartY=25.7233 StartZ=0 EndX=-28.9233 EndY=22.56 EndZ=0
  constraints (26):
    c: Horizontal(g0)
    c: Coincident(g0,g1)
    c: Vertical(g1)
    c: Coincident(g1,g2)
    c: Horizontal(g2)
    c: Coincident(g2,g3)
    c: Vertical(g3)
    c: Coincident(g3,g4)
    c: Horizontal(g4)
    c: Coincident(g4,g5)
    c: Vertical(g5)
    c: Coincident(g5,g6)
    c: Horizontal(g6)
    c: Coincident(g6,g7)
    c: Vertical(g7)
    c: Coincident(g7,g8)
    c: Horizontal(g8)
    c: Coincident(g8,g9)
    c: Coincident(g9,g10)
    c: Vertical(g10)
    c: Coincident(g10,g0)
    c: Vertical(g11)
    c: Coincident(g11,g12)
    c: Horizontal(g12)
    c: Coincident(g12,g13)
    c: Coincident(g13,g11)
FEATURE [PartDesign::Pocket] Pocket001  label="Pocket4"
  BaseFeature = -> Pad008
  Length = 1
  Length2 = 100
  Profile = -> Sketch011
  Type = 0
FEATURE [PartDesign::Body] Body009  label="Size-4"
  Group = -> [Sketch009,Pad008,Sketch011,Pocket001]
  Origin = -> Origin009
  Tip = -> Pocket001
FEATURE [Sketcher::SketchObject] Sketch012  label="Num5"
  AttachmentOffset = pos=(27.25,-10.6,0) rot=(0,0,1;0rad)
  MapMode = 5
  Placement = pos=(27.25,-10.6,4) rot=(0,0,1;0rad)
  Support = -> [Pad009]
  sketch-geometry (26):
    g0: LineSegment StartX=-25.1267 StartY=27.2533 StartZ=0 EndX=-25.1267 EndY=26.4 EndZ=0
    g1: LineSegment StartX=-28.8733 StartY=27.2533 StartZ=0 EndX=-25.1267 EndY=27.2533 EndZ=0
    g2: LineSegment StartX=-29.4167 StartY=23.6267 StartZ=0 EndX=-28.8733 EndY=27.2533 EndZ=0
    g3: LineSegment StartX=-28.5867 StartY=23.6267 StartZ=0 EndX=-29.4167 EndY=23.6267 EndZ=0
    g4: BSplineCurve PolesCount=3 KnotsCount=2 Degree=2 IsPeriodic=0
    g5: BSplineCurve PolesCount=3 KnotsCount=2 Degree=2 IsPeriodic=0
    g6: BSplineCurve PolesCount=3 KnotsCount=2 Degree=2 IsPeriodic=0
    g7: BSplineCurve PolesCount=3 KnotsCount=2 Degree=2 IsPeriodic=0
    g8: BSplineCurve PolesCount=3 KnotsCount=2 Degree=2 IsPeriodic=0
    g9: BSplineCurve PolesCount=3 KnotsCount=2 Degree=2 IsPeriodic=0
    g10: BSplineCurve PolesCount=3 KnotsCount=2 Degree=2 IsPeriodic=0
    g11: LineSegment StartX=-29.64 StartY=21.7067 StartZ=0 EndX=-28.74 EndY=21.7067 EndZ=0
    g12: BSplineCurve PolesCount=3 KnotsCount=2 Degree=2 IsPeriodic=0
    g13: BSplineCurve PolesCount=3 KnotsCount=2 Degree=2 IsPeriodic=0
    g14: BSplineCurve PolesCount=3 KnotsCount=2 Degree=2 IsPeriodic=0
    g15: BSplineCurve PolesCount=3 KnotsCount=2 Degree=2 IsPeriodic=0
    g16: BSplineCurve PolesCount=3 KnotsCount=2 Degree=2 IsPeriodic=0
    g17: BSplineCurve PolesCount=3 KnotsCount=2 Degree=2 IsPeriodic=0
    g18: BSplineCurve PolesCount=3 KnotsCount=2 Degree=2 IsPeriodic=0
    g19: BSplineCurve PolesCount=3 KnotsCount=2 Degree=2 IsPeriodic=0
    g20: BSplineCurve PolesCount=3 KnotsCount=2 Degree=2 IsPeriodic=0
    g21: BSplineCurve PolesCount=3 KnotsCount=2 Degree=2 IsPeriodic=0
    g22: BSplineCurve PolesCount=3 KnotsCount=2 Degree=2 IsPeriodic=0
    g23: BSplineCurve PolesCount=3 KnotsCount=2 Degree=2 IsPeriodic=0
    g24: LineSegment StartX=-28.1467 StartY=26.4 StartZ=0 EndX=-28.4333 EndY=24.3467 EndZ=0
    g25: LineSegment StartX=-25.1267 StartY=26.4 StartZ=0 EndX=-28.1467 EndY=26.4 EndZ=0
  constraints (31):
    c: Vertical(g0)
    c: Coincident(g0,g1)
    c: Horizontal(g1)
    c: Coincident(g1,g2)
    c: Coincident(g2,g3)
    c: Horizontal(g3)
    c: Coincident(g3,g4)
    c: Coincident(g4,g5)
    c: Coincident(g5,g6)
    c: Coincident(g6,g7)
    c: Coincident(g7,g8)
    c: Coincident(g8,g9)
    c: Coincident(g9,g10)
    c: Coincident(g10,g11)
    c: Horizontal(g11)
    c: Coincident(g11,g12)
    c: Coincident(g12,g13)
    c: Coincident(g13,g14)
    c: Coincident(g14,g15)
    c: Coincident(g15,g16)
    c: Coincident(g16,g17)
    c: Coincident(g17,g18)
    c: Coincident(g18,g19)
    c: Coincident(g19,g20)
    c: Coincident(g20,g21)
    c: Coincident(g21,g22)
    c: Coincident(g22,g23)
    c: Coincident(g23,g24)
    c: Coincident(g24,g25)
    c: Horizontal(g25)
    c: Coincident(g25,g0)
FEATURE [PartDesign::Pocket] Pocket002  label="Pocket5"
  BaseFeature = -> Pad009
  Length = 1
  Length2 = 100
  Profile = -> Sketch012
  Type = 0
FEATURE [PartDesign::Body] Body008  label="Size-5"
  Group = -> [Sketch008,Pad009,Sketch012,Pocket002]
  Origin = -> Origin008
  Tip = -> Pocket002
FEATURE [Sketcher::SketchObject] Sketch013  label="Num6"
  AttachmentOffset = pos=(27.15,-10.2,0) rot=(0,0,1;0rad)
  MapMode = 5
  Placement = pos=(27.15,-10.2,4) rot=(0,0,1;0rad)
  Support = -> [Pad006]
  sketch-geometry (26):
    g0: BSplineCurve PolesCount=3 KnotsCount=2 Degree=2 IsPeriodic=0
    g1: BSplineCurve PolesCount=3 KnotsCount=2 Degree=2 IsPeriodic=0
    g2: BSplineCurve PolesCount=3 KnotsCount=2 Degree=2 IsPeriodic=0
    g3: BSplineCurve PolesCount=3 KnotsCount=2 Degree=2 IsPeriodic=0
    g4: BSplineCurve PolesCount=3 KnotsCount=2 Degree=2 IsPeriodic=0
    g5: BSplineCurve PolesCount=3 KnotsCount=2 Degree=2 IsPeriodic=0
    g6: BSplineCurve PolesCount=3 KnotsCount=2 Degree=2 IsPeriodic=0
    g7: BSplineCurve PolesCount=3 KnotsCount=2 Degree=2 IsPeriodic=0
    g8: BSplineCurve PolesCount=3 KnotsCount=2 Degree=2 IsPeriodic=0
    g9: BSplineCurve PolesCount=3 KnotsCount=2 Degree=2 IsPeriodic=0
    g10: BSplineCurve PolesCount=3 KnotsCount=2 Degree=2 IsPeriodic=0
    g11: LineSegment StartX=-24.9 StartY=25.3333 StartZ=0 EndX=-25.8 EndY=25.3333 EndZ=0
    g12: BSplineCurve PolesCount=3 KnotsCount=2 Degree=2 IsPeriodic=0
    g13: BSplineCurve PolesCount=3 KnotsCount=2 Degree=2 IsPeriodic=0
    g14: BSplineCurve PolesCount=3 KnotsCount=2 Degree=2 IsPeriodic=0
    g15: BSplineCurve PolesCount=3 KnotsCount=2 Degree=2 IsPeriodic=0
    g16: BSplineCurve PolesCount=3 KnotsCount=2 Degree=2 IsPeriodic=0
    g17: BSplineCurve PolesCount=3 KnotsCount=2 Degree=2 IsPeriodic=0
    g18: BSplineCurve PolesCount=3 KnotsCount=2 Degree=2 IsPeriodic=0
    g19: BSplineCurve PolesCount=3 KnotsCount=2 Degree=2 IsPeriodic=0
    g20: BSplineCurve PolesCount=3 KnotsCount=2 Degree=2 IsPeriodic=0
    g21: BSplineCurve PolesCount=3 KnotsCount=2 Degree=2 IsPeriodic=0
    g22: BSplineCurve PolesCount=3 KnotsCount=2 Degree=2 IsPeriodic=0
    g23: BSplineCurve PolesCount=3 KnotsCount=2 Degree=2 IsPeriodic=0
    g24: BSplineCurve PolesCount=3 KnotsCount=2 Degree=2 IsPeriodic=0
    g25: BSplineCurve PolesCount=3 KnotsCount=2 Degree=2 IsPeriodic=0
  constraints (27):
    c: Coincident(g0,g1)
    c: Coincident(g1,g2)
    c: Coincident(g2,g3)
    c: Coincident(g3,g4)
    c: Coincident(g4,g5)
    c: Coincident(g5,g6)
    c: Coincident(g6,g7)
    c: Coincident(g7,g8)
    c: Coincident(g8,g9)
    c: Coincident(g9,g10)
    c: Coincident(g10,g11)
    c: Horizontal(g11)
    c: Coincident(g11,g12)
    c: Coincident(g12,g13)
    c: Coincident(g13,g14)
    c: Coincident(g14,g15)
    c: Coincident(g15,g16)
    c: Coincident(g16,g17)
    c: Coincident(g17,g0)
    c: Coincident(g18,g19)
    c: Coincident(g19,g20)
    c: Coincident(g20,g21)
    c: Coincident(g21,g22)
    c: Coincident(g22,g23)
    c: Coincident(g23,g24)
    c: Coincident(g24,g25)
    c: Coincident(g25,g18)
FEATURE [PartDesign::Pocket] Pocket003  label="Pocket6"
  BaseFeature = -> Pad006
  Length = 1
  Length2 = 100
  Profile = -> Sketch013
  Type = 0
FEATURE [PartDesign::Body] Body007  label="Size-6"
  Group = -> [Sketch007,Pad006,Sketch013,Pocket003]
  Origin = -> Origin007
  Tip = -> Pocket003
FEATURE [Sketcher::SketchObject] Sketch014  label="Num7"
  AttachmentOffset = pos=(27.1,-9.8,0) rot=(0,0,1;0rad)
  MapMode = 5
  Placement = pos=(27.1,-9.8,4) rot=(0,0,1;0rad)
  Support = -> [Pad007]
  sketch-geometry (9):
    g0: LineSegment StartX=-24.6767 StartY=27.2533 StartZ=0 EndX=-24.6767 EndY=26.5267 EndZ=0
    g1: LineSegment StartX=-29.53 StartY=27.2533 StartZ=0 EndX=-24.6767 EndY=27.2533 EndZ=0
    g2: LineSegment StartX=-29.53 StartY=26.4 StartZ=0 EndX=-29.53 EndY=27.2533 EndZ=0
    g3: LineSegment StartX=-25.6067 StartY=26.4 StartZ=0 EndX=-29.53 EndY=26.4 EndZ=0
    g4: BSplineCurve PolesCount=3 KnotsCount=2 Degree=2 IsPeriodic=0
    g5: BSplineCurve PolesCount=3 KnotsCount=2 Degree=2 IsPeriodic=0
    g6: LineSegment StartX=-27.6233 StartY=20 StartZ=0 EndX=-28.5867 EndY=20 EndZ=0
    g7: BSplineCurve PolesCount=3 KnotsCount=2 Degree=2 IsPeriodic=0
    g8: BSplineCurve PolesCount=3 KnotsCount=2 Degree=2 IsPeriodic=0
  constraints (14):
    c: Vertical(g0)
    c: Coincident(g0,g1)
    c: Horizontal(g1)
    c: Coincident(g1,g2)
    c: Vertical(g2)
    c: Coincident(g2,g3)
    c: Horizontal(g3)
    c: Coincident(g3,g4)
    c: Coincident(g4,g5)
    c: Coincident(g5,g6)
    c: Horizontal(g6)
    c: Coincident(g6,g7)
    c: Coincident(g7,g8)
    c: Coincident(g8,g0)
FEATURE [PartDesign::Pocket] Pocket004  label="Pocket7"
  BaseFeature = -> Pad007
  Length = 1
  Length2 = 100
  Profile = -> Sketch014
  Type = 0
FEATURE [PartDesign::Body] Body006  label="Size-7"
  Group = -> [Sketch006,Pad007,Sketch014,Pocket004]
  Origin = -> Origin006
  Tip = -> Pocket004
FEATURE [Sketcher::SketchObject] Sketch015  label="Num8"
  AttachmentOffset = pos=(27.2,-9.3,0) rot=(0,0,1;0rad)
  MapMode = 5
  Placement = pos=(27.2,-9.3,4) rot=(0,0,1;0rad)
  Support = -> [Pad004]
  sketch-geometry (30):
    g0: BSplineCurve PolesCount=3 KnotsCount=2 Degree=2 IsPeriodic=0
    g1: BSplineCurve PolesCount=3 KnotsCount=2 Degree=2 IsPeriodic=0
    g2: BSplineCurve PolesCount=3 KnotsCount=2 Degree=2 IsPeriodic=0
    g3: BSplineCurve PolesCount=3 KnotsCount=2 Degree=2 IsPeriodic=0
    g4: BSplineCurve PolesCount=3 KnotsCount=2 Degree=2 IsPeriodic=0
    g5: BSplineCurve PolesCount=3 KnotsCount=2 Degree=2 IsPeriodic=0
    g6: BSplineCurve PolesCount=3 KnotsCount=2 Degree=2 IsPeriodic=0
    g7: BSplineCurve PolesCount=3 KnotsCount=2 Degree=2 IsPeriodic=0
    g8: BSplineCurve PolesCount=3 KnotsCount=2 Degree=2 IsPeriodic=0
    g9: BSplineCurve PolesCount=3 KnotsCount=2 Degree=2 IsPeriodic=0
    g10: BSplineCurve PolesCount=3 KnotsCount=2 Degree=2 IsPeriodic=0
    g11: BSplineCurve PolesCount=3 KnotsCount=2 Degree=2 IsPeriodic=0
    g12: BSplineCurve PolesCount=3 KnotsCount=2 Degree=2 IsPeriodic=0
    g13: BSplineCurve PolesCount=3 KnotsCount=2 Degree=2 IsPeriodic=0
    g14: BSplineCurve PolesCount=3 KnotsCount=2 Degree=2 IsPeriodic=0
    g15: BSplineCurve PolesCount=3 KnotsCount=2 Degree=2 IsPeriodic=0
    g16: BSplineCurve PolesCount=3 KnotsCount=2 Degree=2 IsPeriodic=0
    g17: BSplineCurve PolesCount=3 KnotsCount=2 Degree=2 IsPeriodic=0
    g18: BSplineCurve PolesCount=3 KnotsCount=2 Degree=2 IsPeriodic=0
    g19: BSplineCurve PolesCount=3 KnotsCount=2 Degree=2 IsPeriodic=0
    g20: BSplineCurve PolesCount=3 KnotsCount=2 Degree=2 IsPeriodic=0
    g21: BSplineCurve PolesCount=3 KnotsCount=2 Degree=2 IsPeriodic=0
    g22: BSplineCurve PolesCount=3 KnotsCount=2 Degree=2 IsPeriodic=0
    g23: BSplineCurve PolesCount=3 KnotsCount=2 Degree=2 IsPeriodic=0
    g24: BSplineCurve PolesCount=3 KnotsCount=2 Degree=2 IsPeriodic=0
    g25: BSplineCurve PolesCount=3 KnotsCount=2 Degree=2 IsPeriodic=0
    g26: BSplineCurve PolesCount=3 KnotsCount=2 Degree=2 IsPeriodic=0
    g27: BSplineCurve PolesCount=3 KnotsCount=2 Degree=2 IsPeriodic=0
    g28: BSplineCurve PolesCount=3 KnotsCount=2 Degree=2 IsPeriodic=0
    g29: BSplineCurve PolesCount=3 KnotsCount=2 Degree=2 IsPeriodic=0
  constraints (30):
    c: Coincident(g0,g1)
    c: Coincident(g1,g2)
    c: Coincident(g2,g3)
    c: Coincident(g3,g4)
    c: Coincident(g4,g5)
    c: Coincident(g5,g6)
    c: Coincident(g6,g7)
    c: Coincident(g7,g8)
    c: Coincident(g8,g9)
    c: Coincident(g9,g10)
    c: Coincident(g10,g11)
    c: Coincident(g11,g12)
    c: Coincident(g12,g13)
    c: Coincident(g13,g0)
    c: Coincident(g14,g15)
    c: Coincident(g15,g16)
    c: Coincident(g16,g17)
    c: Coincident(g17,g18)
    c: Coincident(g18,g19)
    c: Coincident(g19,g20)
    c: Coincident(g20,g21)
    c: Coincident(g21,g14)
    c: Coincident(g22,g23)
    c: Coincident(g23,g24)
    c: Coincident(g24,g25)
    c: Coincident(g25,g26)
    c: Coincident(g26,g27)
    c: Coincident(g27,g28)
    c: Coincident(g28,g29)
    c: Coincident(g29,g22)
FEATURE [PartDesign::Pocket] Pocket005  label="Pocket8"
  BaseFeature = -> Pad004
  Length = 1
  Length2 = 100
  Profile = -> Sketch015
  Type = 0
FEATURE [PartDesign::Body] Body005  label="Size-8"
  Group = -> [Sketch005,Pad004,Sketch015,Pocket005]
  Origin = -> Origin005
  Tip = -> Pocket005
FEATURE [Sketcher::SketchObject] Sketch016  label="Num9"
  AttachmentOffset = pos=(27.2,-9,0) rot=(0,0,1;0rad)
  MapMode = 5
  Placement = pos=(27.2,-9,4) rot=(0,0,1;0rad)
  Support = -> [Pad005]
  sketch-geometry (26):
    g0: BSplineCurve PolesCount=3 KnotsCount=2 Degree=2 IsPeriodic=0
    g1: BSplineCurve PolesCount=3 KnotsCount=2 Degree=2 IsPeriodic=0
    g2: BSplineCurve PolesCount=3 KnotsCount=2 Degree=2 IsPeriodic=0
    g3: BSplineCurve PolesCount=3 KnotsCount=2 Degree=2 IsPeriodic=0
    g4: BSplineCurve PolesCount=3 KnotsCount=2 Degree=2 IsPeriodic=0
    g5: BSplineCurve PolesCount=3 KnotsCount=2 Degree=2 IsPeriodic=0
    g6: BSplineCurve PolesCount=3 KnotsCount=2 Degree=2 IsPeriodic=0
    g7: BSplineCurve PolesCount=3 KnotsCount=2 Degree=2 IsPeriodic=0
    g8: BSplineCurve PolesCount=3 KnotsCount=2 Degree=2 IsPeriodic=0
    g9: BSplineCurve PolesCount=3 KnotsCount=2 Degree=2 IsPeriodic=0
    g10: BSplineCurve PolesCount=3 KnotsCount=2 Degree=2 IsPeriodic=0
    g11: LineSegment StartX=-29.4567 StartY=21.4933 StartZ=0 EndX=-28.5567 EndY=21.4933 EndZ=0
    g12: BSplineCurve PolesCount=3 KnotsCount=2 Degree=2 IsPeriodic=0
    g13: BSplineCurve PolesCount=3 KnotsCount=2 Degree=2 IsPeriodic=0
    g14: BSplineCurve PolesCount=3 KnotsCount=2 Degree=2 IsPeriodic=0
    g15: BSplineCurve PolesCount=3 KnotsCount=2 Degree=2 IsPeriodic=0
    g16: BSplineCurve PolesCount=3 KnotsCount=2 Degree=2 IsPeriodic=0
    g17: BSplineCurve PolesCount=3 KnotsCount=2 Degree=2 IsPeriodic=0
    g18: BSplineCurve PolesCount=3 KnotsCount=2 Degree=2 IsPeriodic=0
    g19: BSplineCurve PolesCount=3 KnotsCount=2 Degree=2 IsPeriodic=0
    g20: BSplineCurve PolesCount=3 KnotsCount=2 Degree=2 IsPeriodic=0
    g21: BSplineCurve PolesCount=3 KnotsCount=2 Degree=2 IsPeriodic=0
    g22: BSplineCurve PolesCount=3 KnotsCount=2 Degree=2 IsPeriodic=0
    g23: BSplineCurve PolesCount=3 KnotsCount=2 Degree=2 IsPeriodic=0
    g24: BSplineCurve PolesCount=3 KnotsCount=2 Degree=2 IsPeriodic=0
    g25: BSplineCurve PolesCount=3 KnotsCount=2 Degree=2 IsPeriodic=0
  constraints (27):
    c: Coincident(g0,g1)
    c: Coincident(g1,g2)
    c: Coincident(g2,g3)
    c: Coincident(g3,g4)
    c: Coincident(g4,g5)
    c: Coincident(g5,g6)
    c: Coincident(g6,g7)
    c: Coincident(g7,g8)
    c: Coincident(g8,g9)
    c: Coincident(g9,g10)
    c: Coincident(g10,g11)
    c: Horizontal(g11)
    c: Coincident(g11,g12)
    c: Coincident(g12,g13)
    c: Coincident(g13,g14)
    c: Coincident(g14,g15)
    c: Coincident(g15,g16)
    c: Coincident(g16,g17)
    c: Coincident(g17,g0)
    c: Coincident(g18,g19)
    c: Coincident(g19,g20)
    c: Coincident(g20,g21)
    c: Coincident(g21,g22)
    c: Coincident(g22,g23)
    c: Coincident(g23,g24)
    c: Coincident(g24,g25)
    c: Coincident(g25,g18)
FEATURE [PartDesign::Pocket] Pocket006  label="Pocket9"
  BaseFeature = -> Pad005
  Length = 1
  Length2 = 100
  Profile = -> Sketch016
  Type = 0
FEATURE [PartDesign::Body] Body004  label="Size-9"
  Group = -> [Sketch004,Pad005,Sketch016,Pocket006]
  Origin = -> Origin004
  Tip = -> Pocket006
FEATURE [Sketcher::SketchObject] Sketch017  label="Num10"
  AttachmentOffset = pos=(24,-8.6,0) rot=(0,0,1;0rad)
  MapMode = 5
  Placement = pos=(24,-8.6,4) rot=(0,0,1;0rad)
  Support = -> [Pad002]
  sketch-geometry (23):
    g0: LineSegment StartX=-27.3467 StartY=25.12 StartZ=0 EndX=-28.9567 EndY=25.12 EndZ=0
    g1: LineSegment StartX=-27.3467 StartY=20 StartZ=0 EndX=-27.3467 EndY=25.12 EndZ=0
    g2: LineSegment StartX=-26.4467 StartY=20 StartZ=0 EndX=-27.3467 EndY=20 EndZ=0
    g3: LineSegment StartX=-26.4467 StartY=27.2533 StartZ=0 EndX=-26.4467 EndY=20 EndZ=0
    g4: LineSegment StartX=-27.04 StartY=27.2533 StartZ=0 EndX=-26.4467 EndY=27.2533 EndZ=0
    g5: BSplineCurve PolesCount=3 KnotsCount=2 Degree=2 IsPeriodic=0
    g6: BSplineCurve PolesCount=3 KnotsCount=2 Degree=2 IsPeriodic=0
    g7: LineSegment StartX=-28.9567 StartY=25.12 StartZ=0 EndX=-28.9567 EndY=25.76 EndZ=0
    g8: BSplineCurve PolesCount=3 KnotsCount=2 Degree=2 IsPeriodic=0
    g9: BSplineCurve PolesCount=3 KnotsCount=2 Degree=2 IsPeriodic=0
    g10: BSplineCurve PolesCount=3 KnotsCount=2 Degree=2 IsPeriodic=0
    g11: BSplineCurve PolesCount=3 KnotsCount=2 Degree=2 IsPeriodic=0
    g12: BSplineCurve PolesCount=3 KnotsCount=2 Degree=2 IsPeriodic=0
    g13: BSplineCurve PolesCount=3 KnotsCount=2 Degree=2 IsPeriodic=0
    g14: BSplineCurve PolesCount=3 KnotsCount=2 Degree=2 IsPeriodic=0
    g15: BSplineCurve PolesCount=3 KnotsCount=2 Degree=2 IsPeriodic=0
    g16: BSplineCurve PolesCount=3 KnotsCount=2 Degree=2 IsPeriodic=0
    g17: BSplineCurve PolesCount=3 KnotsCount=2 Degree=2 IsPeriodic=0
    g18: BSplineCurve PolesCount=3 KnotsCount=2 Degree=2 IsPeriodic=0
    g19: BSplineCurve PolesCount=3 KnotsCount=2 Degree=2 IsPeriodic=0
    g20: BSplineCurve PolesCount=3 KnotsCount=2 Degree=2 IsPeriodic=0
    g21: BSplineCurve PolesCount=3 KnotsCount=2 Degree=2 IsPeriodic=0
    g22: BSplineCurve PolesCount=3 KnotsCount=2 Degree=2 IsPeriodic=0
  constraints (29):
    c: Horizontal(g0)
    c: Coincident(g0,g1)
    c: Vertical(g1)
    c: Coincident(g1,g2)
    c: Horizontal(g2)
    c: Coincident(g2,g3)
    c: Vertical(g3)
    c: Coincident(g3,g4)
    c: Horizontal(g4)
    c: Coincident(g4,g5)
    c: Coincident(g5,g6)
    c: Coincident(g6,g7)
    c: Vertical(g7)
    c: Coincident(g7,g0)
    c: Coincident(g8,g9)
    c: Coincident(g9,g10)
    c: Coincident(g10,g11)
    c: Coincident(g11,g12)
    c: Coincident(g12,g13)
    c: Coincident(g13,g14)
    c: Coincident(g14,g15)
    c: Coincident(g15,g16)
    c: Coincident(g16,g17)
    c: Coincident(g17,g8)
    c: Coincident(g18,g19)
    c: Coincident(g19,g20)
    c: Coincident(g20,g21)
    c: Coincident(g21,g22)
    c: Coincident(g22,g18)
FEATURE [PartDesign::Pocket] Pocket007  label="Pocket10"
  BaseFeature = -> Pad002
  Length = 1
  Length2 = 100
  Profile = -> Sketch017
  Type = 0
FEATURE [PartDesign::Body] Body003  label="Size-10"
  Group = -> [Sketch003,Pad002,Sketch017,Pocket007]
  Origin = -> Origin003
  Tip = -> Pocket007
FEATURE [Sketcher::SketchObject] Sketch018  label="Num11"
  AttachmentOffset = pos=(24.8,-8.3,0) rot=(0,0,1;0rad)
  MapMode = 5
  Placement = pos=(24.8,-8.3,4) rot=(0,0,1;0rad)
  Support = -> [Pad003]
  sketch-geometry (16):
    g0: LineSegment StartX=-27.3467 StartY=25.12 StartZ=0 EndX=-28.9567 EndY=25.12 EndZ=0
    g1: LineSegment StartX=-27.3467 StartY=20 StartZ=0 EndX=-27.3467 EndY=25.12 EndZ=0
    g2: LineSegment StartX=-26.4467 StartY=20 StartZ=0 EndX=-27.3467 EndY=20 EndZ=0
    g3: LineSegment StartX=-26.4467 StartY=27.2533 StartZ=0 EndX=-26.4467 EndY=20 EndZ=0
    g4: LineSegment StartX=-27.04 StartY=27.2533 StartZ=0 EndX=-26.4467 EndY=27.2533 EndZ=0
    g5: BSplineCurve PolesCount=3 KnotsCount=2 Degree=2 IsPeriodic=0
    g6: BSplineCurve PolesCount=3 KnotsCount=2 Degree=2 IsPeriodic=0
    g7: LineSegment StartX=-28.9567 StartY=25.12 StartZ=0 EndX=-28.9567 EndY=25.76 EndZ=0
    g8: LineSegment StartX=-21.5867 StartY=25.12 StartZ=0 EndX=-23.1967 EndY=25.12 EndZ=0
    g9: LineSegment StartX=-21.5867 StartY=20 StartZ=0 EndX=-21.5867 EndY=25.12 EndZ=0
    g10: LineSegment StartX=-20.6867 StartY=20 StartZ=0 EndX=-21.5867 EndY=20 EndZ=0
    g11: LineSegment StartX=-20.6867 StartY=27.2533 StartZ=0 EndX=-20.6867 EndY=20 EndZ=0
    g12: LineSegment StartX=-21.28 StartY=27.2533 StartZ=0 EndX=-20.6867 EndY=27.2533 EndZ=0
    g13: BSplineCurve PolesCount=3 KnotsCount=2 Degree=2 IsPeriodic=0
    g14: BSplineCurve PolesCount=3 KnotsCount=2 Degree=2 IsPeriodic=0
    g15: LineSegment StartX=-23.1967 StartY=25.12 StartZ=0 EndX=-23.1967 EndY=25.76 EndZ=0
  constraints (28):
    c: Horizontal(g0)
    c: Coincident(g0,g1)
    c: Vertical(g1)
    c: Coincident(g1,g2)
    c: Horizontal(g2)
    c: Coincident(g2,g3)
    c: Vertical(g3)
    c: Coincident(g3,g4)
    c: Horizontal(g4)
    c: Coincident(g4,g5)
    c: Coincident(g5,g6)
    c: Coincident(g6,g7)
    c: Vertical(g7)
    c: Coincident(g7,g0)
    c: Horizontal(g8)
    c: Coincident(g8,g9)
    c: Vertical(g9)
    c: Coincident(g9,g10)
    c: Horizontal(g10)
    c: Coincident(g10,g11)
    c: Vertical(g11)
    c: Coincident(g11,g12)
    c: Horizontal(g12)
    c: Coincident(g12,g13)
    c: Coincident(g13,g14)
    c: Coincident(g14,g15)
    c: Vertical(g15)
    c: Coincident(g15,g8)
FEATURE [PartDesign::Pocket] Pocket010  label="Pocket11"
  BaseFeature = -> Pad003
  Length = 1
  Length2 = 100
  Profile = -> Sketch018
  Type = 0
FEATURE [PartDesign::Body] Body002  label="Size-11"
  Group = -> [Sketch002,Pad003,Sketch018,Pocket010]
  Origin = -> Origin002
  Tip = -> Pocket010
FEATURE [Sketcher::SketchObject] Sketch019  label="Num12"
  AttachmentOffset = pos=(24,-7.8,0) rot=(0,0,1;0rad)
  MapMode = 5
  Placement = pos=(24,-7.8,4) rot=(0,0,1;0rad)
  Support = -> [Pad001]
  sketch-geometry (26):
    g0: LineSegment StartX=-27.3467 StartY=25.12 StartZ=0 EndX=-28.9567 EndY=25.12 EndZ=0
    g1: LineSegment StartX=-27.3467 StartY=20 StartZ=0 EndX=-27.3467 EndY=25.12 EndZ=0
    g2: LineSegment StartX=-26.4467 StartY=20 StartZ=0 EndX=-27.3467 EndY=20 EndZ=0
    g3: LineSegment StartX=-26.4467 StartY=27.2533 StartZ=0 EndX=-26.4467 EndY=20 EndZ=0
    g4: LineSegment StartX=-27.04 StartY=27.2533 StartZ=0 EndX=-26.4467 EndY=27.2533 EndZ=0
    g5: BSplineCurve PolesCount=3 KnotsCount=2 Degree=2 IsPeriodic=0
    g6: BSplineCurve PolesCount=3 KnotsCount=2 Degree=2 IsPeriodic=0
    g7: LineSegment StartX=-28.9567 StartY=25.12 StartZ=0 EndX=-28.9567 EndY=25.76 EndZ=0
    g8: BSplineCurve PolesCount=3 KnotsCount=2 Degree=2 IsPeriodic=0
    g9: LineSegment StartX=-22.8267 StartY=24.9067 StartZ=0 EndX=-23.7267 EndY=24.9067 EndZ=0
    g10: BSplineCurve PolesCount=3 KnotsCount=2 Degree=2 IsPeriodic=0
    g11: BSplineCurve PolesCount=3 KnotsCount=2 Degree=2 IsPeriodic=0
    g12: BSplineCurve PolesCount=3 KnotsCount=2 Degree=2 IsPeriodic=0
    g13: BSplineCurve PolesCount=3 KnotsCount=2 Degree=2 IsPeriodic=0
    g14: LineSegment StartX=-21.8533 StartY=23.0933 StartZ=0 EndX=-20.9133 EndY=23.6233 EndZ=0
    g15: BSplineCurve PolesCount=3 KnotsCount=2 Degree=2 IsPeriodic=0
    g16: BSplineCurve PolesCount=3 KnotsCount=2 Degree=2 IsPeriodic=0
    g17: LineSegment StartX=-19.06 StartY=20 StartZ=0 EndX=-23.8933 EndY=20 EndZ=0
    g18: LineSegment StartX=-19.06 StartY=20.8533 StartZ=0 EndX=-19.06 EndY=20 EndZ=0
    g19: LineSegment StartX=-22.8767 StartY=20.8533 StartZ=0 EndX=-19.06 EndY=20.8533 EndZ=0
    g20: BSplineCurve PolesCount=3 KnotsCount=2 Degree=2 IsPeriodic=0
    g21: BSplineCurve PolesCount=3 KnotsCount=2 Degree=2 IsPeriodic=0
    g22: LineSegment StartX=-20.5433 StartY=22.89 StartZ=0 EndX=-21.5667 EndY=22.34 EndZ=0
    g23: BSplineCurve PolesCount=3 KnotsCount=2 Degree=2 IsPeriodic=0
    g24: BSplineCurve PolesCount=3 KnotsCount=2 Degree=2 IsPeriodic=0
    g25: BSplineCurve PolesCount=3 KnotsCount=2 Degree=2 IsPeriodic=0
  constraints (36):
    c: Horizontal(g0)
    c: Coincident(g0,g1)
    c: Vertical(g1)
    c: Coincident(g1,g2)
    c: Horizontal(g2)
    c: Coincident(g2,g3)
    c: Vertical(g3)
    c: Coincident(g3,g4)
    c: Horizontal(g4)
    c: Coincident(g4,g5)
    c: Coincident(g5,g6)
    c: Coincident(g6,g7)
    c: Vertical(g7)
    c: Coincident(g7,g0)
    c: Coincident(g8,g9)
    c: Horizontal(g9)
    c: Coincident(g9,g10)
    c: Coincident(g10,g11)
    c: Coincident(g11,g12)
    c: Coincident(g12,g13)
    c: Coincident(g13,g14)
    c: Coincident(g14,g15)
    c: Coincident(g15,g16)
    c: Coincident(g16,g17)
    c: Horizontal(g17)
    c: Coincident(g17,g18)
    c: Vertical(g18)
    c: Coincident(g18,g19)
    c: Horizontal(g19)
    c: Coincident(g19,g20)
    c: Coincident(g20,g21)
    c: Coincident(g21,g22)
    c: Coincident(g22,g23)
    c: Coincident(g23,g24)
    c: Coincident(g24,g25)
    c: Coincident(g25,g8)
FEATURE [PartDesign::Pocket] Pocket011  label="Pocket12"
  BaseFeature = -> Pad001
  Length = 1
  Length2 = 100
  Profile = -> Sketch019
  Type = 0
FEATURE [PartDesign::Body] Body001  label="Size-12"
  Group = -> [Sketch001,Pad001,Sketch019,Pocket011]
  Origin = -> Origin001
  Tip = -> Pocket011
FEATURE [Sketcher::SketchObject] Sketch020  label="Num13"
  AttachmentOffset = pos=(24,-6.2,0) rot=(0,0,1;0rad)
  MapMode = 5
  Placement = pos=(24,-6.2,4) rot=(0,0,1;0rad)
  Support = -> [Pad]
  sketch-geometry (33):
    g0: LineSegment StartX=-27.3467 StartY=25.12 StartZ=0 EndX=-28.9567 EndY=25.12 EndZ=0
    g1: LineSegment StartX=-27.3467 StartY=20 StartZ=0 EndX=-27.3467 EndY=25.12 EndZ=0
    g2: LineSegment StartX=-26.4467 StartY=20 StartZ=0 EndX=-27.3467 EndY=20 EndZ=0
    g3: LineSegment StartX=-26.4467 StartY=27.2533 StartZ=0 EndX=-26.4467 EndY=20 EndZ=0
    g4: LineSegment StartX=-27.04 StartY=27.2533 StartZ=0 EndX=-26.4467 EndY=27.2533 EndZ=0
    g5: BSplineCurve PolesCount=3 KnotsCount=2 Degree=2 IsPeriodic=0
    g6: BSplineCurve PolesCount=3 KnotsCount=2 Degree=2 IsPeriodic=0
    g7: LineSegment StartX=-28.9567 StartY=25.12 StartZ=0 EndX=-28.9567 EndY=25.76 EndZ=0
    g8: BSplineCurve PolesCount=3 KnotsCount=2 Degree=2 IsPeriodic=0
    g9: BSplineCurve PolesCount=3 KnotsCount=2 Degree=2 IsPeriodic=0
    g10: BSplineCurve PolesCount=3 KnotsCount=2 Degree=2 IsPeriodic=0
    g11: BSplineCurve PolesCount=3 KnotsCount=2 Degree=2 IsPeriodic=0
    g12: BSplineCurve PolesCount=3 KnotsCount=2 Degree=2 IsPeriodic=0
    g13: LineSegment StartX=-21.9767 StartY=23.4133 StartZ=0 EndX=-21.9767 EndY=24.2667 EndZ=0
    g14: LineSegment StartX=-21.8633 StartY=23.4133 StartZ=0 EndX=-21.9767 EndY=23.4133 EndZ=0
    g15: LineSegment StartX=-21.4833 StartY=23.4233 StartZ=0 EndX=-21.8633 EndY=23.4133 EndZ=0
    g16: BSplineCurve PolesCount=3 KnotsCount=2 Degree=2 IsPeriodic=0
    g17: BSplineCurve PolesCount=3 KnotsCount=2 Degree=2 IsPeriodic=0
    g18: BSplineCurve PolesCount=3 KnotsCount=2 Degree=2 IsPeriodic=0
    g19: BSplineCurve PolesCount=3 KnotsCount=2 Degree=2 IsPeriodic=0
    g20: BSplineCurve PolesCount=3 KnotsCount=2 Degree=2 IsPeriodic=0
    g21: LineSegment StartX=-23.9133 StartY=21.92 StartZ=0 EndX=-23.01 EndY=21.92 EndZ=0
    g22: BSplineCurve PolesCount=3 KnotsCount=2 Degree=2 IsPeriodic=0
    g23: BSplineCurve PolesCount=3 KnotsCount=2 Degree=2 IsPeriodic=0
    g24: BSplineCurve PolesCount=3 KnotsCount=2 Degree=2 IsPeriodic=0
    g25: BSplineCurve PolesCount=3 KnotsCount=2 Degree=2 IsPeriodic=0
    g26: BSplineCurve PolesCount=3 KnotsCount=2 Degree=2 IsPeriodic=0
    g27: BSplineCurve PolesCount=3 KnotsCount=2 Degree=2 IsPeriodic=0
    g28: BSplineCurve PolesCount=3 KnotsCount=2 Degree=2 IsPeriodic=0
    g29: BSplineCurve PolesCount=3 KnotsCount=2 Degree=2 IsPeriodic=0
    g30: BSplineCurve PolesCount=3 KnotsCount=2 Degree=2 IsPeriodic=0
    g31: LineSegment StartX=-22.8567 StartY=25.12 StartZ=0 EndX=-23.76 EndY=25.12 EndZ=0
    g32: BSplineCurve PolesCount=3 KnotsCount=2 Degree=2 IsPeriodic=0
  constraints (43):
    c: Horizontal(g0)
    c: Coincident(g0,g1)
    c: Vertical(g1)
    c: Coincident(g1,g2)
    c: Horizontal(g2)
    c: Coincident(g2,g3)
    c: Vertical(g3)
    c: Coincident(g3,g4)
    c: Horizontal(g4)
    c: Coincident(g4,g5)
    c: Coincident(g5,g6)
    c: Coincident(g6,g7)
    c: Vertical(g7)
    c: Coincident(g7,g0)
    c: Coincident(g8,g9)
    c: Coincident(g9,g10)
    c: Coincident(g10,g11)
    c: Coincident(g11,g12)
    c: Coincident(g12,g13)
    c: Vertical(g13)
    c: Coincident(g13,g14)
    c: Horizontal(g14)
    c: Coincident(g14,g15)
    c: Coincident(g15,g16)
    c: Coincident(g16,g17)
    c: Coincident(g17,g18)
    c: Coincident(g18,g19)
    c: Coincident(g19,g20)
    c: Coincident(g20,g21)
    c: Horizontal(g21)
    c: Coincident(g21,g22)
    c: Coincident(g22,g23)
    c: Coincident(g23,g24)
    c: Coincident(g24,g25)
    c: Coincident(g25,g26)
    c: Coincident(g26,g27)
    c: Coincident(g27,g28)
    c: Coincident(g28,g29)
    c: Coincident(g29,g30)
    c: Coincident(g30,g31)
    c: Horizontal(g31)
    c: Coincident(g31,g32)
    c: Coincident(g32,g8)
FEATURE [PartDesign::Pocket] Pocket012  label="Pocket13"
  BaseFeature = -> Pad
  Length = 1
  Length2 = 100
  Profile = -> Sketch020
  Type = 0
FEATURE [PartDesign::Body] Body  label="Size-13"
  Group = -> [Sketch,Pad,Sketch020,Pocket012]
  Origin = -> Origin
  Tip = -> Pocket012
FEATURE [Mesh::Feature] Mesh  label="Size-13 (Meshed)"
FEATURE [Mesh::Feature] Mesh001  label="Size-12 (Meshed)"
FEATURE [Mesh::Feature] Mesh002  label="Size-11 (Meshed)"
FEATURE [Mesh::Feature] Mesh003  label="Size-10 (Meshed)"
FEATURE [Mesh::Feature] Mesh004  label="Size-9 (Meshed)"
FEATURE [Mesh::Feature] Mesh005  label="Size-8 (Meshed)"
FEATURE [Mesh::Feature] Mesh006  label="Size-7 (Meshed)"
FEATURE [Mesh::Feature] Mesh007  label="Size-6 (Meshed)"
FEATURE [Mesh::Feature] Mesh008  label="Size-5 (Meshed)"
FEATURE [Mesh::Feature] Mesh009  label="Size-4 (Meshed)"
FEATURE [Mesh::Feature] Mesh010  label="Size-3 (Meshed)"
note: 1 file-system path scrubbed to <path> (originals preserved in the JSON sidecar)
